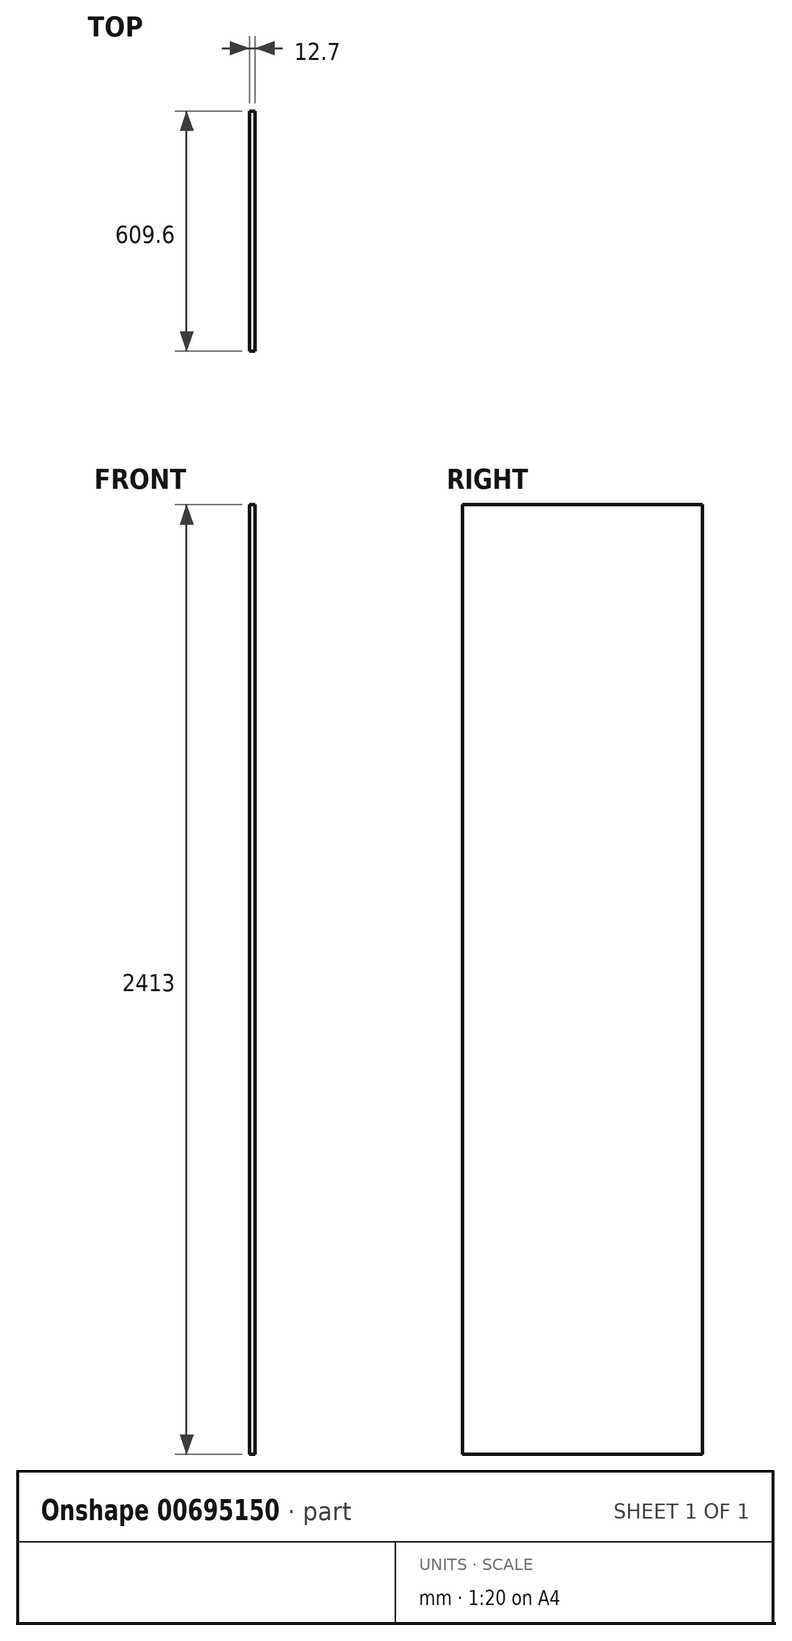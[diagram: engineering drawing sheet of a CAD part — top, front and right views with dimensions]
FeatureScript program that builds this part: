
annotation { "Feature Type Name" : "Feature", "Feature Type Description" : "" }
export const myFeature = defineFeature(function(context is Context, id is Id, definition is map)
    precondition{}
    {
        {
            var Q0;
            Q0=qCreatedBy(makeId("Top.planeOp"),FACE);
            var sketch = newSketch(context, id + "F0", { "sketchPlane" : qUnion([Q0])});
            skLineSegment(sketch, "E0.bottom", {"start": v(804.17, 2598.13) * mm, "end": v(816.87, 2598.13) * mm});
            skLineSegment(sketch, "E0.top", {"start": v(804.17, 1988.53) * mm, "end": v(816.87, 1988.53) * mm});
            skLineSegment(sketch, "E0.left", {"start": v(804.17, 2598.13) * mm, "end": v(804.17, 1988.53) * mm});
            skLineSegment(sketch, "E0.right", {"start": v(816.87, 2598.13) * mm, "end": v(816.87, 1988.53) * mm});
            skSolve(sketch);
        }
        {
            var Q0;
            Q0=makeQuery(id+"F0.imprint","IMPRINT",FACE,{"disambiguationData":[TD([[makeQuery(id+"F0.imprint","IMPRINT",EDGE,{"derivedFrom":sQuery(id+"F0.wireOp",EDGE,"E0.bottom")}),-1.0]])]});
            extrude(context, id + "F1", {"entities" : qUnion([Q0]), "depth" : 2413 * mm, "offsetDistance" : 25.4 * mm});
        }
    });
